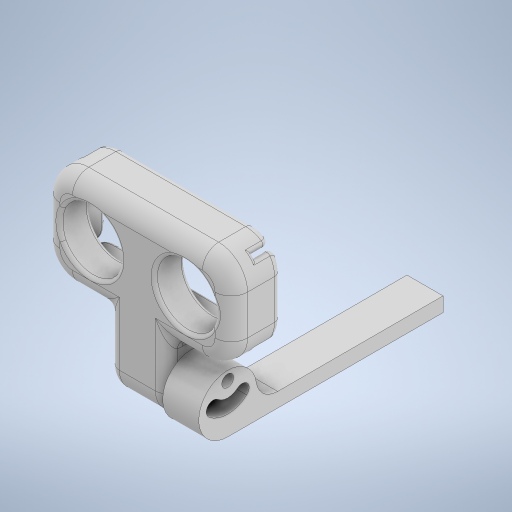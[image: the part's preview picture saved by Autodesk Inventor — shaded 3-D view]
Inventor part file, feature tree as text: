
AUTODESK INVENTOR PART (.ipt)
format: ipt  version: 2023 (Build 270158030, 158C)  size: 1,049,088 bytes
history: native  units: mm
features: fillet x19, extrude x12, sketch x12, other x3, projected_geometry x2
ambient origin geometry x8: Origin, YZ Plane, XZ Plane, XY Plane, X Axis, Y Axis, Z Axis, Center Point
bodies: Body1 (feature_tree), Body2 (feature_tree), Body3 (feature_tree)
feature tree (48):
  other  "Ping Sensor Base"
  extrude  "Extrusion1"  Depth=3.0mm TaperAngle=0.0deg
  extrude  "Extrusion2"  Depth=3.0mm TaperAngle=0.0deg
  extrude  "Extrusion3"  Depth=1.55mm
  fillet  "Fillet1"  Radius=12.0mm
  extrude  "Extrusion4"  Depth=14.0mm
  extrude  "Extrusion6"  Depth=1.5mm
  fillet  "Fillet9"  Radius=7.0mm
  fillet  "Fillet10"  Radius=7.0mm
  fillet  "Fillet11"  [1 undecoded]
  fillet  "Fillet12"  Radius=15.0mm
  fillet  "Fillet15"  Radius=6.0mm
  fillet  "Fillet16"  Radius=15.0mm
  extrude  "Extrusion7"  Depth=30.0mm
  extrude  "Extrusion8"  Depth=3.1mm
  extrude  "Extrusion9"  Depth=3.0mm
  extrude  "Extrusion10"  Depth=8.2mm
  fillet  "Fillet17"  Radius=10.2mm
  fillet  "Fillet18"  Radius=8.2mm
  fillet  "Fillet19"  Radius=10.2mm
  fillet  "Fillet20"  Radius=7.5mm
  fillet  "Fillet21"  Radius=7.5mm
  fillet  "Fillet22"  [1 undecoded]
  extrude  "Extrusion11"  Depth=7.0mm
  fillet  "Fillet27"  Radius=2.0mm
  extrude  "Extrusion13"  Depth=2.0mm
  fillet  "Fillet29"  Radius=3.0mm
  fillet  "Fillet30"  Radius=17.0mm
  fillet  "Fillet31"  Radius=30.0mm
  fillet  "Fillet32"  Radius=10.0mm
  fillet  "Fillet33"  Radius=27.0mm
  extrude  "Extrusion14"  Depth=26.0mm
  sketch  "Sketch1"  dims[d0=36.0mm d1=3.0mm d2=0.0mm]
  sketch  "Sketch2"  dims[d3=3.1mm d4=3.0mm d5=0.0mm]
  sketch  "Sketch3"  dims[d7=3.1mm d8=1.55mm d9=12.0mm]
  sketch  "Sketch4"  dims[d10=3.0mm d11=0.0mm d15=14.0mm]
  sketch  "Sketch6"  dims[d16=3.5mm d17=1.5mm]
  sketch  "Sketch7"  dims[d18=2.5mm d19=6.5mm d20=20.0mm d21=0.0mm d22=7.0mm d23=7.0mm d24=0.0mm d25=15.0mm d37=6.0mm d54=15.0mm]
  other  "Ping Sensor Housing"
  sketch  "Sketch8"  dims[d55=15.0mm d56=30.0mm]
  sketch  "Sketch9"  dims[d57=3.0mm d58=3.1mm]
  sketch  "Sketch10"  dims[d59=4.5mm d60=3.0mm]
  sketch  "Sketch11"  dims[d61=3.1mm d62=8.2mm d63=10.2mm d64=8.2mm d65=10.2mm d66=7.5mm d67=7.5mm d68=0.0mm d69=0.0mm]
  sketch  "Sketch13"  dims[d70=1.5mm d71=7.0mm d72=2.0mm]
  sketch  "Sketch14"  dims[d73=1.0mm d76=2.0mm d77=3.0mm d78=17.0mm d79=30.0mm d80=10.0mm d81=0.0mm d82=27.0mm d83=26.0mm d84=26.0mm d85=10.0mm d86=0.0mm d87=45.8mm d88=20.8mm d89=3.1mm d90=3.1mm d91=3.1mm d92=3.1mm d93=5.5mm d94=0.0mm d95=17.0mm d96=17.0mm d97=9.75mm d99=9.75mm d100=10.0mm d101=10.0mm d102=9.3mm d103=0.0mm d104=0.0mm d105=8.0mm d106=4.5mm d107=2.0mm d108=7.0mm d109=3.0mm d110=3.0mm d111=3.1mm d112=3.1mm d113=6.1mm d114=0.0mm d115=0.0mm d116=4.0mm d118=4.0mm d135=0.9mm d137=0.0mm d138=6.0mm d139=5.0mm d140=5.0mm d141=4.0mm d142=3.0mm d143=0.0mm d144=1.0mm d145=0.3mm d146=1.0mm d147=26.3mm d148=43.3mm d149=1.0mm d150=1.0mm d160=1.0mm d161=67.7mm d162=4.0mm d163=6.0mm d164=4.0mm d165=4.0mm d166=0.1mm d167=0.4mm d168=10.0mm d169=0.0mm]
  projected_geometry  "Projected Loop1"
  projected_geometry  "Projected Loop2"
  other  "hoz-mount"
note: 2 required parameter values undecoded (feature->parameter linkage not recoverable at this tier; creation-order binding heuristic only, values carry confidence <= 0.55)
